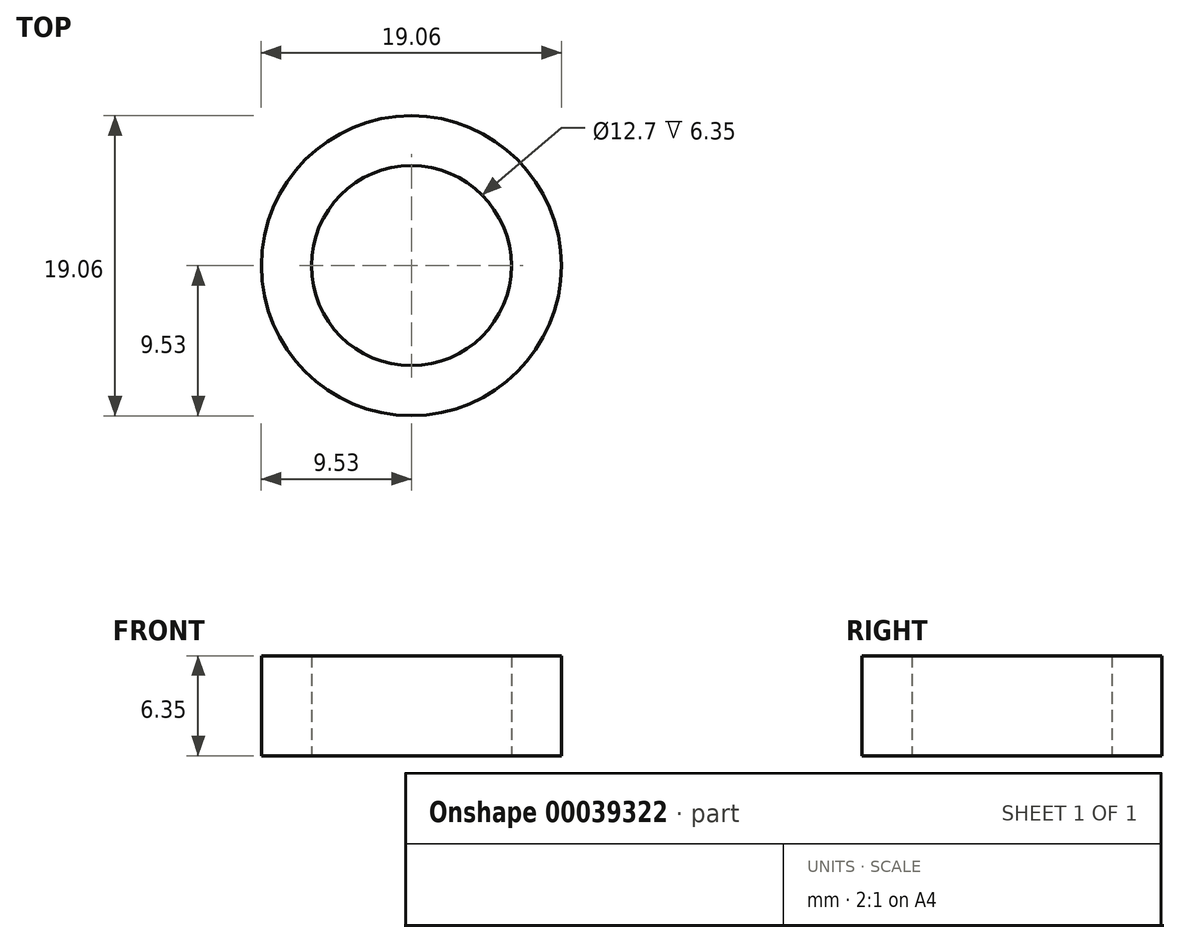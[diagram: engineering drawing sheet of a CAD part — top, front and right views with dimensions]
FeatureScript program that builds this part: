
annotation { "Feature Type Name" : "Feature", "Feature Type Description" : "" }
export const myFeature = defineFeature(function(context is Context, id is Id, definition is map)
    precondition{}
    {
        {
            var Q0;
            Q0=qCreatedBy(makeId("Top.planeOp"),FACE);
            var sketch = newSketch(context, id + "F0", { "sketchPlane" : qUnion([Q0])});
            skCircle(sketch, "E0", {"center": v(0, 0) * mm, "radius": 9.53 * mm});
            skCircle(sketch, "E1.0", {"center": v(0, 0) * mm, "radius": 6.35 * mm});
            skSolve(sketch);
        }
        {
            var Q0;
            Q0 = qSketchRegion(id + "F0", true);
            extrude(context, id + "F1", {"entities" : qUnion([Q0]), "depth" : 6.35 * mm});
        }
    });
